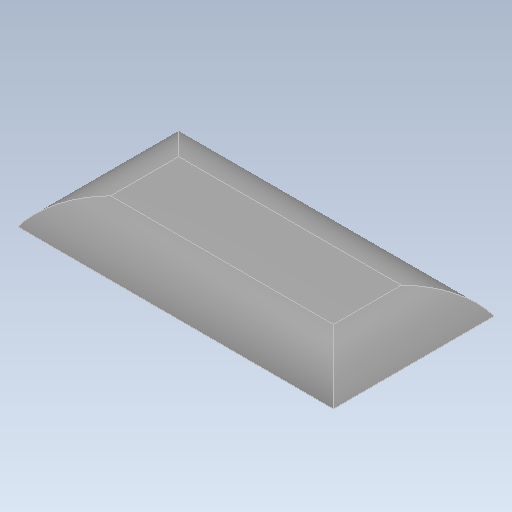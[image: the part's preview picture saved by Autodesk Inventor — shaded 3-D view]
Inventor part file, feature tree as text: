
AUTODESK INVENTOR PART (.ipt)
format: ipt  version: 2021 (Build 250183000, 183)  size: 100,352 bytes
history: mixed  units: mm
features: other x1, fillet x1, imported_body x1
ambient origin geometry x8: Origin, YZ Plane, XZ Plane, XY Plane, X Axis, Y Axis, Z Axis, Center Point
bodies: Body1 (imported_parasolid)
feature tree (3):
  other  "Sólido1"
  fillet  "Fillet1"  [1 undecoded]
  imported_body  NMx_Import_Brep_tag  [imported B-rep: ~6 faces, bbox_mm=[58.87, 5.0, 30.0]]
note: 1 required parameter value undecoded (feature->parameter linkage not recoverable at this tier; creation-order binding heuristic only, values carry confidence <= 0.55)
